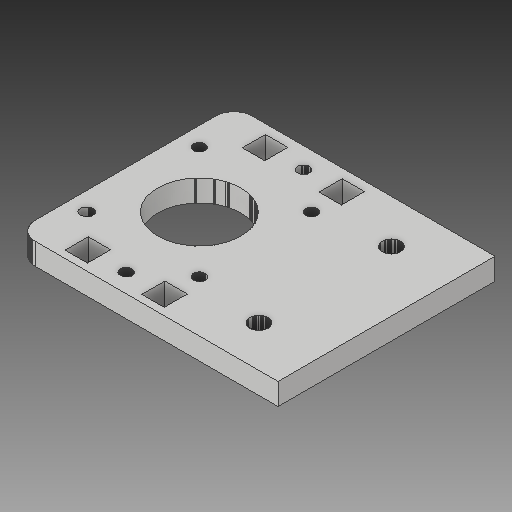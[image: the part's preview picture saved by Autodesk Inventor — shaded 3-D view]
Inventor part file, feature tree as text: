
AUTODESK INVENTOR PART (.ipt)
format: ipt  version: 2018 (Build 220112000, 112)  size: 1,148,928 bytes
history: native  units: mm
features: sketch x4, extrude x2, hole x2
ambient origin geometry x8: Origin, YZ Plane, XZ Plane, XY Plane, X Axis, Y Axis, Z Axis, Center Point
bodies: Solid1 (feature_tree)
feature tree (8):
  extrude  "Extrusion1"  Depth=10.0mm TaperAngle=0.0deg
  hole  "Hole1"  [1 undecoded]
  hole  "Hole2"  [1 undecoded]
  extrude  "Extrusion2"  [1 undecoded]
  sketch  "Sketch1"  dims[d0=6.0mm d1=0.0mm]
  sketch  "Sketch2"  dims[d2=3.2mm d3=6.0mm d4=4.0mm d5=2.0mm d6=90.0deg d7=8.0mm d8=20.594885mm]
  sketch  "Sketch3"  dims[d9=5.0mm d10=6.0mm d11=4.0mm d12=2.0mm d13=90.0deg d14=8.0mm d15=20.594885mm d16=10.0mm d17=0.0mm]
  sketch  "Sketch4"
note: 3 required parameter values undecoded (feature->parameter linkage not recoverable at this tier; creation-order binding heuristic only, values carry confidence <= 0.55)
